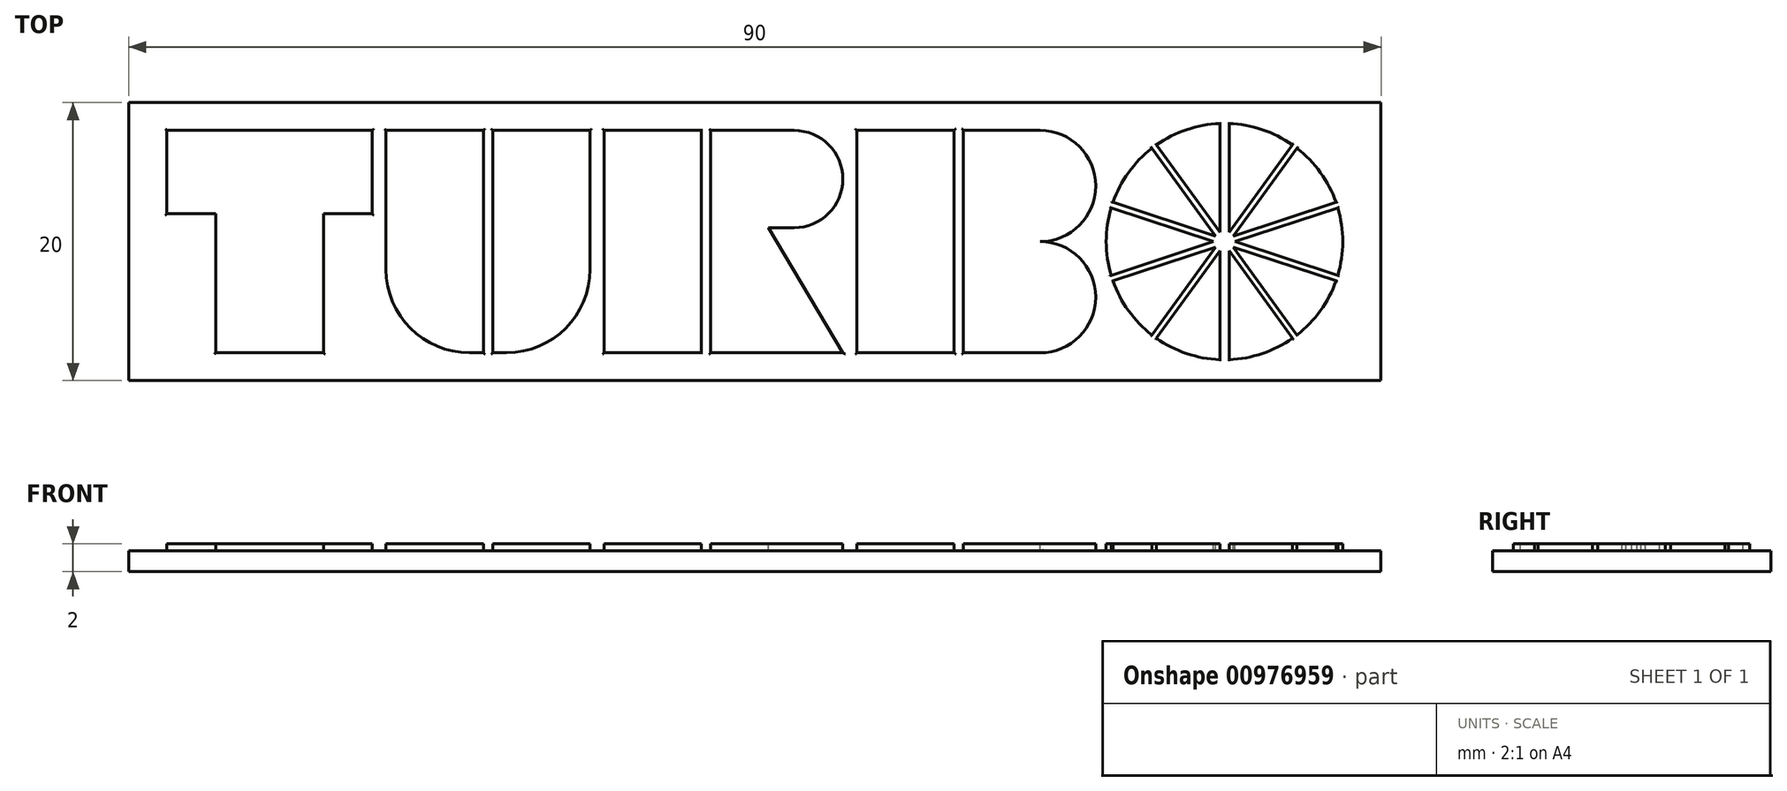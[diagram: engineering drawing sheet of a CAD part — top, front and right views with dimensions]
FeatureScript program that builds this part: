
annotation { "Feature Type Name" : "Feature", "Feature Type Description" : "" }
export const myFeature = defineFeature(function(context is Context, id is Id, definition is map)
    precondition{}
    {
        {
            var Q0;
            Q0=qCreatedBy(makeId("Top.planeOp"),FACE);
            var sketch = newSketch(context, id + "F0", { "sketchPlane" : qUnion([Q0])});
            skLineSegment(sketch, "E0.bottom", {"start": v(-37.82, -15.3) * mm, "end": v(52.18, -15.3) * mm});
            skLineSegment(sketch, "E0.top", {"start": v(-37.82, 4.7) * mm, "end": v(52.18, 4.7) * mm});
            skLineSegment(sketch, "E0.left", {"start": v(-37.82, -15.3) * mm, "end": v(-37.82, 4.7) * mm});
            skLineSegment(sketch, "E0.right", {"start": v(52.18, -15.3) * mm, "end": v(52.18, 4.7) * mm});
            skLineSegment(sketch, "E1", {"start": v(-20.58, -13.3) * mm, "end": v(-20.58, -7.3) * mm});
            skLineSegment(sketch, "E2", {"start": v(-20.58, -7.3) * mm, "end": v(-24.08, -7.3) * mm});
            skLineSegment(sketch, "E3", {"start": v(-24.08, -7.3) * mm, "end": v(-24.08, 2.7) * mm});
            skLineSegment(sketch, "E4", {"start": v(-24.08, 2.7) * mm, "end": v(-31.82, 2.7) * mm});
            skLineSegment(sketch, "E5", {"start": v(-31.82, 2.7) * mm, "end": v(-31.82, -7.3) * mm});
            skLineSegment(sketch, "E6", {"start": v(-31.82, -7.3) * mm, "end": v(-35.32, -7.3) * mm});
            skLineSegment(sketch, "E7", {"start": v(-35.32, -7.3) * mm, "end": v(-35.32, -13.3) * mm});
            skLineSegment(sketch, "E8", {"start": v(-35.32, -13.3) * mm, "end": v(-20.58, -13.3) * mm});
            skLineSegment(sketch, "E9.bottom", {"start": v(-19.58, -13.3) * mm, "end": v(-12.58, -13.3) * mm});
            skLineSegment(sketch, "E9.top", {"start": v(-13.58, 2.7) * mm, "end": v(-12.58, 2.7) * mm});
            skLineSegment(sketch, "E9.left", {"start": v(-19.58, -13.3) * mm, "end": v(-19.58, -3.3) * mm});
            skLineSegment(sketch, "E9.right", {"start": v(-12.58, -13.3) * mm, "end": v(-12.58, 2.7) * mm});
            skPoint(sketch, "E10.visualSharp", {"position": v(-19.58, 2.7) * mm});
            skArc(sketch, "E10.filletArc", {"start": v(-13.58, 2.7) * mm, "mid": v(-17.82, 0.94) * mm, "end": v(-19.58, -3.3) * mm});
            skLineSegment(sketch, "E11.bottom", {"start": v(-11.91, -13.3) * mm, "end": v(-4.91, -13.3) * mm});
            skLineSegment(sketch, "E11.top", {"start": v(-11.91, 2.7) * mm, "end": v(-10.91, 2.7) * mm});
            skLineSegment(sketch, "E11.left", {"start": v(-11.91, -13.3) * mm, "end": v(-11.91, 2.7) * mm});
            skLineSegment(sketch, "E11.right", {"start": v(-4.91, -13.3) * mm, "end": v(-4.91, -3.3) * mm});
            skPoint(sketch, "E12.visualSharp", {"position": v(-4.91, 2.7) * mm});
            skArc(sketch, "E12.filletArc", {"start": v(-4.91, -3.3) * mm, "mid": v(-6.67, 0.94) * mm, "end": v(-10.91, 2.7) * mm});
            skLineSegment(sketch, "E13.bottom", {"start": v(-3.91, -13.3) * mm, "end": v(3.09, -13.3) * mm});
            skLineSegment(sketch, "E13.top", {"start": v(-3.91, 2.7) * mm, "end": v(3.09, 2.7) * mm});
            skLineSegment(sketch, "E13.left", {"start": v(-3.91, -13.3) * mm, "end": v(-3.91, 2.7) * mm});
            skLineSegment(sketch, "E13.right", {"start": v(3.09, -13.3) * mm, "end": v(3.09, 2.7) * mm});
            skLineSegment(sketch, "E14", {"start": v(3.76, -13.3) * mm, "end": v(3.76, 2.7) * mm});
            skLineSegment(sketch, "E15", {"start": v(3.76, 2.7) * mm, "end": v(13.26, 2.7) * mm});
            skLineSegment(sketch, "E16", {"start": v(13.26, 2.7) * mm, "end": v(7.91, -6.3) * mm});
            skLineSegment(sketch, "E17.bottom", {"start": v(3.76, -13.3) * mm, "end": v(9.76, -13.3) * mm});
            skLineSegment(sketch, "E17.top", {"start": v(7.91, -6.3) * mm, "end": v(9.76, -6.3) * mm});
            skLineSegment(sketch, "E17.left", {"start": v(3.76, -13.3) * mm, "end": v(3.76, -6.3) * mm});
            skLineSegment(sketch, "E17.right", {"start": v(13.26, -9.8) * mm, "end": v(13.26, -9.8) * mm});
            skPoint(sketch, "E18.visualSharp", {"position": v(13.26, -13.3) * mm});
            skArc(sketch, "E18.filletArc", {"start": v(9.76, -13.3) * mm, "mid": v(12.23, -12.28) * mm, "end": v(13.26, -9.8) * mm});
            skPoint(sketch, "E19.visualSharp", {"position": v(13.26, -6.3) * mm});
            skArc(sketch, "E19.filletArc", {"start": v(13.26, -9.8) * mm, "mid": v(12.23, -7.33) * mm, "end": v(9.76, -6.3) * mm});
            skLineSegment(sketch, "E20.bottom", {"start": v(14.26, -13.3) * mm, "end": v(21.26, -13.3) * mm});
            skLineSegment(sketch, "E20.top", {"start": v(14.26, 2.7) * mm, "end": v(21.26, 2.7) * mm});
            skLineSegment(sketch, "E20.left", {"start": v(14.26, -13.3) * mm, "end": v(14.26, 2.7) * mm});
            skLineSegment(sketch, "E20.right", {"start": v(21.26, -13.3) * mm, "end": v(21.26, 2.7) * mm});
            skLineSegment(sketch, "E21.bottom", {"start": v(21.92, -13.3) * mm, "end": v(27.42, -13.3) * mm});
            skLineSegment(sketch, "E21.left", {"start": v(21.92, -13.3) * mm, "end": v(21.92, -5.3) * mm});
            skLineSegment(sketch, "E21.right", {"start": v(31.42, -9.3) * mm, "end": v(31.42, -9.3) * mm});
            skLineSegment(sketch, "E22.top", {"start": v(21.92, 2.7) * mm, "end": v(27.42, 2.7) * mm});
            skLineSegment(sketch, "E22.left", {"start": v(21.92, -5.3) * mm, "end": v(21.92, 2.7) * mm});
            skLineSegment(sketch, "E22.right", {"start": v(31.42, -1.3) * mm, "end": v(31.42, -1.3) * mm});
            skPoint(sketch, "E23.visualSharp", {"position": v(31.42, -13.3) * mm});
            skArc(sketch, "E23.filletArc", {"start": v(27.42, -13.3) * mm, "mid": v(30.25, -12.14) * mm, "end": v(31.42, -9.3) * mm});
            skPoint(sketch, "E24.visualSharp", {"position": v(31.42, -5.3) * mm});
            skArc(sketch, "E24.filletArc", {"start": v(31.42, -9.3) * mm, "mid": v(30.25, -6.48) * mm, "end": v(27.42, -5.3) * mm});
            skArc(sketch, "E25.filletArc", {"start": v(27.42, -5.3) * mm, "mid": v(30.25, -4.14) * mm, "end": v(31.42, -1.3) * mm});
            skPoint(sketch, "E26.visualSharp", {"position": v(31.42, 2.7) * mm});
            skArc(sketch, "E26.filletArc", {"start": v(31.42, -1.3) * mm, "mid": v(30.25, 1.52) * mm, "end": v(27.42, 2.7) * mm});
            skArc(sketch, "E27", {"start": v(41.01, -13.8) * mm, "mid": v(43.4, -13.36) * mm, "end": v(45.56, -12.27) * mm});
            skArc(sketch, "E28", {"start": v(39.93, -5.3) * mm, "mid": v(39.93, -5.3) * mm, "end": v(39.93, -5.32) * mm});
            skLineSegment(sketch, "E29", {"start": v(40.68, 4.7) * mm, "end": v(40.68, 8.95) * mm, "construction": true});
            skLineSegment(sketch, "E30.left", {"start": v(40.34, -13.8) * mm, "end": v(40.34, -5.98) * mm});
            skLineSegment(sketch, "E30.right", {"start": v(41.01, -13.8) * mm, "end": v(41.01, -5.98) * mm});
            skLineSegment(sketch, "E31.trimOffspring", {"start": v(40.34, -4.64) * mm, "end": v(40.34, 3.19) * mm});
            skLineSegment(sketch, "E32.trimOffspring", {"start": v(41.01, -4.64) * mm, "end": v(41.01, 3.19) * mm});
            skArc(sketch, "E33.trimOffspring", {"start": v(40.34, 3.19) * mm, "mid": v(37.96, 2.75) * mm, "end": v(35.8, 1.65) * mm});
            skLineSegment(sketch, "E34", {"start": v(41.01, -4.64) * mm, "end": v(45.56, 1.65) * mm});
            skLineSegment(sketch, "E35", {"start": v(41.01, -5.98) * mm, "end": v(45.56, -12.27) * mm});
            skLineSegment(sketch, "E36", {"start": v(40.34, -5.98) * mm, "end": v(35.8, -12.27) * mm});
            skLineSegment(sketch, "E37", {"start": v(40.34, -4.64) * mm, "end": v(35.8, 1.65) * mm});
            skLineSegment(sketch, "E38", {"start": v(41.31, -4.91) * mm, "end": v(45.89, 1.4) * mm});
            skLineSegment(sketch, "E39", {"start": v(41.31, -4.91) * mm, "end": v(48.7, -2.49) * mm});
            skLineSegment(sketch, "E40", {"start": v(40.04, -4.91) * mm, "end": v(35.47, 1.4) * mm});
            skLineSegment(sketch, "E41", {"start": v(40.04, -4.91) * mm, "end": v(32.66, -2.49) * mm});
            skLineSegment(sketch, "E42", {"start": v(45.89, -12.02) * mm, "end": v(41.31, -5.7) * mm});
            skLineSegment(sketch, "E43", {"start": v(40.04, -5.7) * mm, "end": v(35.47, -12.02) * mm});
            skLineSegment(sketch, "E44", {"start": v(41.31, -5.7) * mm, "end": v(48.7, -8.13) * mm});
            skLineSegment(sketch, "E45", {"start": v(40.04, -5.7) * mm, "end": v(32.66, -8.13) * mm});
            skLineSegment(sketch, "E46", {"start": v(41.43, -5.3) * mm, "end": v(48.82, -7.74) * mm});
            skLineSegment(sketch, "E47", {"start": v(41.43, -5.3) * mm, "end": v(48.82, -2.87) * mm});
            skLineSegment(sketch, "E48", {"start": v(39.93, -5.3) * mm, "end": v(32.53, -7.73) * mm});
            skLineSegment(sketch, "E49", {"start": v(32.53, -2.89) * mm, "end": v(39.93, -5.32) * mm});
            skArc(sketch, "E50.trimOffspring", {"start": v(35.8, -12.27) * mm, "mid": v(37.96, -13.36) * mm, "end": v(40.34, -13.8) * mm});
            skArc(sketch, "E51.trimOffspring", {"start": v(32.66, -8.13) * mm, "mid": v(33.78, -10.28) * mm, "end": v(35.47, -12.02) * mm});
            skArc(sketch, "E52.trimOffspring", {"start": v(32.53, -2.89) * mm, "mid": v(32.18, -5.3) * mm, "end": v(32.53, -7.73) * mm});
            skArc(sketch, "E53.trimOffspring", {"start": v(45.89, -12.02) * mm, "mid": v(47.57, -10.28) * mm, "end": v(48.7, -8.13) * mm});
            skArc(sketch, "E54.trimOffspring", {"start": v(48.82, -7.74) * mm, "mid": v(49.18, -5.3) * mm, "end": v(48.82, -2.87) * mm});
            skArc(sketch, "E55.trimOffspring", {"start": v(48.7, -2.49) * mm, "mid": v(47.57, -0.34) * mm, "end": v(45.89, 1.4) * mm});
            skArc(sketch, "E56.trimOffspring", {"start": v(45.56, 1.65) * mm, "mid": v(43.4, 2.75) * mm, "end": v(41.01, 3.19) * mm});
            skArc(sketch, "E57.trimOffspring", {"start": v(35.47, 1.4) * mm, "mid": v(33.78, -0.34) * mm, "end": v(32.66, -2.49) * mm});
            skSolve(sketch);
        }
        {
            var Q0;
            Q0=makeQuery(id+"F0.imprint","IMPRINT",FACE,{"disambiguationData":[TD([[makeQuery(id+"F0.imprint","IMPRINT",EDGE,{"derivedFrom":sQuery(id+"F0.wireOp",EDGE,"E1")}),1.0]])]});
            var Q1;
            Q1=makeQuery(id+"F0.imprint","IMPRINT",FACE,{"disambiguationData":[TD([[makeQuery(id+"F0.imprint","IMPRINT",EDGE,{"derivedFrom":sQuery(id+"F0.wireOp",EDGE,"E9.bottom")}),1.0]])]});
            var Q2;
            Q2=makeQuery(id+"F0.imprint","IMPRINT",FACE,{"disambiguationData":[TD([[makeQuery(id+"F0.imprint","IMPRINT",EDGE,{"derivedFrom":sQuery(id+"F0.wireOp",EDGE,"E11.bottom")}),1.0]])]});
            var Q3;
            Q3=makeQuery(id+"F0.imprint","IMPRINT",FACE,{"disambiguationData":[TD([[makeQuery(id+"F0.imprint","IMPRINT",EDGE,{"derivedFrom":sQuery(id+"F0.wireOp",EDGE,"E13.bottom")}),1.0]])]});
            var Q4;
            Q4=makeQuery(id+"F0.imprint","IMPRINT",FACE,{"disambiguationData":[TD([[makeQuery(id+"F0.imprint","IMPRINT",EDGE,{"derivedFrom":sQuery(id+"F0.wireOp",EDGE,"E14")}),-1.0]])]});
            var Q5;
            Q5=makeQuery(id+"F0.imprint","IMPRINT",FACE,{"disambiguationData":[TD([[makeQuery(id+"F0.imprint","IMPRINT",EDGE,{"derivedFrom":sQuery(id+"F0.wireOp",EDGE,"E20.bottom")}),1.0]])]});
            var Q6;
            Q6=makeQuery(id+"F0.imprint","IMPRINT",FACE,{"disambiguationData":[TD([[makeQuery(id+"F0.imprint","IMPRINT",EDGE,{"derivedFrom":sQuery(id+"F0.wireOp",EDGE,"E22.bottom")}),1.0]])]});
            var Q7;
            Q7=makeQuery(id+"F0.imprint","IMPRINT",FACE,{"disambiguationData":[TD([[makeQuery(id+"F0.imprint","IMPRINT",EDGE,{"derivedFrom":sQuery(id+"F0.wireOp",EDGE,"E21.bottom")}),1.0]])]});
            var Q8;
            Q8=makeQuery(id+"F0.imprint","IMPRINT",FACE,{"disambiguationData":[TD([[makeQuery(id+"F0.imprint","IMPRINT",EDGE,{"derivedFrom":sQuery(id+"F0.wireOp",EDGE,"E31.trimOffspring")}),1.0]])]});
            var Q9;
            Q9=makeQuery(id+"F0.imprint","IMPRINT",FACE,{"disambiguationData":[TD([[makeQuery(id+"F0.imprint","IMPRINT",EDGE,{"derivedFrom":sQuery(id+"F0.wireOp",EDGE,"E40")}),1.0]])]});
            var Q10;
            {var subQ0=sQuery(id+"F0.wireOp",EDGE,"E52.trimOffspring");Q10=makeQuery(id+"F0.imprint","IMPRINT",FACE,{"disambiguationData":[TD([[makeQuery(id+"F0.imprint","IMPRINT",EDGE,{"derivedFrom":subQ0}),1.0]])]});}
            var Q11;
            Q11=makeQuery(id+"F0.imprint","IMPRINT",FACE,{"disambiguationData":[TD([[makeQuery(id+"F0.imprint","IMPRINT",EDGE,{"derivedFrom":sQuery(id+"F0.wireOp",EDGE,"E43")}),-1.0]])]});
            var Q12;
            Q12=makeQuery(id+"F0.imprint","IMPRINT",FACE,{"disambiguationData":[TD([[makeQuery(id+"F0.imprint","IMPRINT",EDGE,{"derivedFrom":sQuery(id+"F0.wireOp",EDGE,"E30.left")}),1.0]])]});
            var Q13;
            Q13=makeQuery(id+"F0.imprint","IMPRINT",FACE,{"disambiguationData":[TD([[makeQuery(id+"F0.imprint","IMPRINT",EDGE,{"derivedFrom":sQuery(id+"F0.wireOp",EDGE,"E27")}),1.0]])]});
            var Q14;
            Q14=makeQuery(id+"F0.imprint","IMPRINT",FACE,{"disambiguationData":[TD([[makeQuery(id+"F0.imprint","IMPRINT",EDGE,{"derivedFrom":sQuery(id+"F0.wireOp",EDGE,"E42")}),-1.0]])]});
            var Q15;
            Q15=makeQuery(id+"F0.imprint","IMPRINT",FACE,{"disambiguationData":[TD([[makeQuery(id+"F0.imprint","IMPRINT",EDGE,{"derivedFrom":sQuery(id+"F0.wireOp",EDGE,"E46")}),1.0]])]});
            var Q16;
            Q16=makeQuery(id+"F0.imprint","IMPRINT",FACE,{"disambiguationData":[TD([[makeQuery(id+"F0.imprint","IMPRINT",EDGE,{"derivedFrom":sQuery(id+"F0.wireOp",EDGE,"E38")}),-1.0]])]});
            var Q17;
            Q17=makeQuery(id+"F0.imprint","IMPRINT",FACE,{"disambiguationData":[TD([[makeQuery(id+"F0.imprint","IMPRINT",EDGE,{"derivedFrom":sQuery(id+"F0.wireOp",EDGE,"E32.trimOffspring")}),-1.0]])]});
            extrude(context, id + "F1", {"entities" : qUnion([Q0, Q1, Q2, Q3, Q4, Q5, Q6, Q7, Q8, Q9, Q10, Q11, Q12, Q13, Q14, Q15, Q16, Q17]), "depth" : 2 * mm, "offsetDistance" : 25 * mm});
        }
        {
            var Q0;
            Q0=makeQuery(id+"F1.opExtrude","CAP_FACE",FACE,{"disambiguationData":[OSD([sQuery(id+"F0.wireOp",EDGE,"E20.bottom"),sQuery(id+"F0.wireOp",EDGE,"E20.top"),sQuery(id+"F0.wireOp",EDGE,"E20.left"),sQuery(id+"F0.wireOp",EDGE,"E20.right")])],"isStart":false});
            cPlane(context, id + "F2", {"entities" : qUnion([Q0]), "cplaneType" : CPlaneType.OFFSET, "offset" : 0 * mm, "width" : 150 * mm, "height" : 150 * mm});
        }
        {
            var Q0;
            Q0=qCreatedBy(id+"F2.planeOp",FACE);
            var sketch = newSketch(context, id + "F3", { "sketchPlane" : qUnion([Q0])});
            skLineSegment(sketch, "E58.bottom", {"start": v(-38.07, 4.7) * mm, "end": v(51.93, 4.7) * mm});
            skLineSegment(sketch, "E58.top", {"start": v(-38.07, -15.3) * mm, "end": v(51.93, -15.3) * mm});
            skLineSegment(sketch, "E58.left", {"start": v(-38.07, 4.7) * mm, "end": v(-38.07, -15.3) * mm});
            skLineSegment(sketch, "E58.right", {"start": v(51.93, 4.7) * mm, "end": v(51.93, -15.3) * mm});
            skSolve(sketch);
        }
        {
            var Q0;
            Q0 = qSketchRegion(id + "F3", true);
            extrude(context, id + "F4", {"entities" : qUnion([Q0]), "depth" : -1.5 * mm, "offsetDistance" : 25 * mm});
        }
        {
            var Q0;
            Q0=makeQuery(id+"F1.opExtrude","SWEPT_BODY",BODY,{"disambiguationData":[OSD([sQuery(id+"F0.wireOp",EDGE,"E1"),sQuery(id+"F0.wireOp",EDGE,"E2"),sQuery(id+"F0.wireOp",EDGE,"E3"),sQuery(id+"F0.wireOp",EDGE,"E4"),sQuery(id+"F0.wireOp",EDGE,"E5"),sQuery(id+"F0.wireOp",EDGE,"E6"),sQuery(id+"F0.wireOp",EDGE,"E7"),sQuery(id+"F0.wireOp",EDGE,"E8")])]});
            var Q1;
            Q1=makeQuery(id+"F1.opExtrude","SWEPT_BODY",BODY,{"disambiguationData":[OSD([sQuery(id+"F0.wireOp",EDGE,"E9.bottom"),sQuery(id+"F0.wireOp",EDGE,"E9.top"),sQuery(id+"F0.wireOp",EDGE,"E9.left"),sQuery(id+"F0.wireOp",EDGE,"E9.right"),sQuery(id+"F0.wireOp",EDGE,"E10.filletArc")])]});
            var Q2;
            Q2=makeQuery(id+"F1.opExtrude","SWEPT_BODY",BODY,{"disambiguationData":[OSD([sQuery(id+"F0.wireOp",EDGE,"E11.bottom"),sQuery(id+"F0.wireOp",EDGE,"E11.top"),sQuery(id+"F0.wireOp",EDGE,"E11.left"),sQuery(id+"F0.wireOp",EDGE,"E11.right"),sQuery(id+"F0.wireOp",EDGE,"E12.filletArc")])]});
            var Q3;
            Q3=makeQuery(id+"F1.opExtrude","SWEPT_BODY",BODY,{"disambiguationData":[OSD([sQuery(id+"F0.wireOp",EDGE,"E13.bottom"),sQuery(id+"F0.wireOp",EDGE,"E13.top"),sQuery(id+"F0.wireOp",EDGE,"E13.left"),sQuery(id+"F0.wireOp",EDGE,"E13.right")])]});
            var Q4;
            Q4=makeQuery(id+"F1.opExtrude","SWEPT_BODY",BODY,{"disambiguationData":[OSD([sQuery(id+"F0.wireOp",EDGE,"E14"),sQuery(id+"F0.wireOp",EDGE,"E15"),sQuery(id+"F0.wireOp",EDGE,"E16"),sQuery(id+"F0.wireOp",EDGE,"E17.bottom"),sQuery(id+"F0.wireOp",EDGE,"E17.top"),sQuery(id+"F0.wireOp",EDGE,"E17.left"),sQuery(id+"F0.wireOp",EDGE,"E18.filletArc"),sQuery(id+"F0.wireOp",EDGE,"E19.filletArc")])]});
            var Q5;
            Q5=makeQuery(id+"F1.opExtrude","SWEPT_BODY",BODY,{"disambiguationData":[OSD([sQuery(id+"F0.wireOp",EDGE,"E20.bottom"),sQuery(id+"F0.wireOp",EDGE,"E20.top"),sQuery(id+"F0.wireOp",EDGE,"E20.left"),sQuery(id+"F0.wireOp",EDGE,"E20.right")])]});
            var Q6;
            Q6=makeQuery(id+"F1.opExtrude","SWEPT_BODY",BODY,{"disambiguationData":[OSD([sQuery(id+"F0.wireOp",EDGE,"E21.bottom"),sQuery(id+"F0.wireOp",EDGE,"E21.left"),sQuery(id+"F0.wireOp",EDGE,"E22.top"),sQuery(id+"F0.wireOp",EDGE,"E22.left"),sQuery(id+"F0.wireOp",EDGE,"E23.filletArc"),sQuery(id+"F0.wireOp",EDGE,"E24.filletArc"),sQuery(id+"F0.wireOp",EDGE,"E25.filletArc"),sQuery(id+"F0.wireOp",EDGE,"E26.filletArc")])]});
            var Q7;
            Q7=makeQuery(id+"F1.opExtrude","SWEPT_BODY",BODY,{"disambiguationData":[OSD([sQuery(id+"F0.wireOp",EDGE,"E27"),sQuery(id+"F0.wireOp",EDGE,"E30.right"),sQuery(id+"F0.wireOp",EDGE,"E35")])]});
            var Q8;
            Q8=makeQuery(id+"F1.opExtrude","SWEPT_BODY",BODY,{"disambiguationData":[OSD([sQuery(id+"F0.wireOp",EDGE,"E30.left"),sQuery(id+"F0.wireOp",EDGE,"E36"),sQuery(id+"F0.wireOp",EDGE,"E50.trimOffspring")])]});
            var Q9;
            Q9=makeQuery(id+"F1.opExtrude","SWEPT_BODY",BODY,{"disambiguationData":[OSD([sQuery(id+"F0.wireOp",EDGE,"E31.trimOffspring"),sQuery(id+"F0.wireOp",EDGE,"E33.trimOffspring"),sQuery(id+"F0.wireOp",EDGE,"E37")])]});
            var Q10;
            Q10=makeQuery(id+"F1.opExtrude","SWEPT_BODY",BODY,{"disambiguationData":[OSD([sQuery(id+"F0.wireOp",EDGE,"E32.trimOffspring"),sQuery(id+"F0.wireOp",EDGE,"E34"),sQuery(id+"F0.wireOp",EDGE,"E56.trimOffspring")])]});
            var Q11;
            Q11=makeQuery(id+"F1.opExtrude","SWEPT_BODY",BODY,{"disambiguationData":[OSD([sQuery(id+"F0.wireOp",EDGE,"E38"),sQuery(id+"F0.wireOp",EDGE,"E39"),sQuery(id+"F0.wireOp",EDGE,"E55.trimOffspring")])]});
            var Q12;
            Q12=makeQuery(id+"F1.opExtrude","SWEPT_BODY",BODY,{"disambiguationData":[OSD([sQuery(id+"F0.wireOp",EDGE,"E40"),sQuery(id+"F0.wireOp",EDGE,"E41"),sQuery(id+"F0.wireOp",EDGE,"E57.trimOffspring")])]});
            var Q13;
            Q13=makeQuery(id+"F1.opExtrude","SWEPT_BODY",BODY,{"disambiguationData":[OSD([sQuery(id+"F0.wireOp",EDGE,"E42"),sQuery(id+"F0.wireOp",EDGE,"E44"),sQuery(id+"F0.wireOp",EDGE,"E53.trimOffspring")])]});
            var Q14;
            Q14=makeQuery(id+"F1.opExtrude","SWEPT_BODY",BODY,{"disambiguationData":[OSD([sQuery(id+"F0.wireOp",EDGE,"E43"),sQuery(id+"F0.wireOp",EDGE,"E45"),sQuery(id+"F0.wireOp",EDGE,"E51.trimOffspring")])]});
            var Q15;
            Q15=makeQuery(id+"F1.opExtrude","SWEPT_BODY",BODY,{"disambiguationData":[OSD([sQuery(id+"F0.wireOp",EDGE,"E46"),sQuery(id+"F0.wireOp",EDGE,"E47"),sQuery(id+"F0.wireOp",EDGE,"E54.trimOffspring")])]});
            var Q16;
            Q16=makeQuery(id+"F1.opExtrude","SWEPT_BODY",BODY,{"disambiguationData":[OSD([sQuery(id+"F0.wireOp",EDGE,"E48"),sQuery(id+"F0.wireOp",EDGE,"E49"),sQuery(id+"F0.wireOp",EDGE,"E52.trimOffspring")])]});
            var Q17;
            Q17=makeQuery(id+"F4.opExtrude","SWEPT_BODY",BODY,{"disambiguationData":[OSD([sQuery(id+"F3.wireOp",EDGE,"E58.bottom"),sQuery(id+"F3.wireOp",EDGE,"E58.top"),sQuery(id+"F3.wireOp",EDGE,"E58.left"),sQuery(id+"F3.wireOp",EDGE,"E58.right")])]});
            transform(context, id + "F5", {"entities" : qUnion([Q0, Q1, Q2, Q3, Q4, Q5, Q6, Q7, Q8, Q9, Q10, Q11, Q12, Q13, Q14, Q15, Q16, Q17]), "transformType" : TransformType.TRANSLATION_3D, "dx" : 0 * mm, "dy" : 0 * mm, "dz" : 0 * mm, "makeCopy" : false});
        }
        {
            var Q0;
            Q0=makeQuery(id+"F1.opExtrude","SWEPT_BODY",BODY,{"disambiguationData":[OSD([sQuery(id+"F0.wireOp",EDGE,"E1"),sQuery(id+"F0.wireOp",EDGE,"E2"),sQuery(id+"F0.wireOp",EDGE,"E3"),sQuery(id+"F0.wireOp",EDGE,"E4"),sQuery(id+"F0.wireOp",EDGE,"E5"),sQuery(id+"F0.wireOp",EDGE,"E6"),sQuery(id+"F0.wireOp",EDGE,"E7"),sQuery(id+"F0.wireOp",EDGE,"E8")])]});
            var Q1;
            Q1=makeQuery(id+"F1.opExtrude","SWEPT_BODY",BODY,{"disambiguationData":[OSD([sQuery(id+"F0.wireOp",EDGE,"E9.bottom"),sQuery(id+"F0.wireOp",EDGE,"E9.top"),sQuery(id+"F0.wireOp",EDGE,"E9.left"),sQuery(id+"F0.wireOp",EDGE,"E9.right"),sQuery(id+"F0.wireOp",EDGE,"E10.filletArc")])]});
            var Q2;
            Q2=makeQuery(id+"F1.opExtrude","SWEPT_BODY",BODY,{"disambiguationData":[OSD([sQuery(id+"F0.wireOp",EDGE,"E11.bottom"),sQuery(id+"F0.wireOp",EDGE,"E11.top"),sQuery(id+"F0.wireOp",EDGE,"E11.left"),sQuery(id+"F0.wireOp",EDGE,"E11.right"),sQuery(id+"F0.wireOp",EDGE,"E12.filletArc")])]});
            var Q3;
            Q3=makeQuery(id+"F1.opExtrude","SWEPT_BODY",BODY,{"disambiguationData":[OSD([sQuery(id+"F0.wireOp",EDGE,"E13.bottom"),sQuery(id+"F0.wireOp",EDGE,"E13.top"),sQuery(id+"F0.wireOp",EDGE,"E13.left"),sQuery(id+"F0.wireOp",EDGE,"E13.right")])]});
            var Q4;
            Q4=makeQuery(id+"F1.opExtrude","SWEPT_BODY",BODY,{"disambiguationData":[OSD([sQuery(id+"F0.wireOp",EDGE,"E14"),sQuery(id+"F0.wireOp",EDGE,"E15"),sQuery(id+"F0.wireOp",EDGE,"E16"),sQuery(id+"F0.wireOp",EDGE,"E17.bottom"),sQuery(id+"F0.wireOp",EDGE,"E17.top"),sQuery(id+"F0.wireOp",EDGE,"E17.left"),sQuery(id+"F0.wireOp",EDGE,"E18.filletArc"),sQuery(id+"F0.wireOp",EDGE,"E19.filletArc")])]});
            var Q5;
            Q5=makeQuery(id+"F1.opExtrude","SWEPT_BODY",BODY,{"disambiguationData":[OSD([sQuery(id+"F0.wireOp",EDGE,"E20.bottom"),sQuery(id+"F0.wireOp",EDGE,"E20.top"),sQuery(id+"F0.wireOp",EDGE,"E20.left"),sQuery(id+"F0.wireOp",EDGE,"E20.right")])]});
            var Q6;
            Q6=makeQuery(id+"F1.opExtrude","SWEPT_BODY",BODY,{"disambiguationData":[OSD([sQuery(id+"F0.wireOp",EDGE,"E21.bottom"),sQuery(id+"F0.wireOp",EDGE,"E21.left"),sQuery(id+"F0.wireOp",EDGE,"E22.top"),sQuery(id+"F0.wireOp",EDGE,"E22.left"),sQuery(id+"F0.wireOp",EDGE,"E23.filletArc"),sQuery(id+"F0.wireOp",EDGE,"E24.filletArc"),sQuery(id+"F0.wireOp",EDGE,"E25.filletArc"),sQuery(id+"F0.wireOp",EDGE,"E26.filletArc")])]});
            var Q7;
            Q7=makeQuery(id+"F1.opExtrude","SWEPT_BODY",BODY,{"disambiguationData":[OSD([sQuery(id+"F0.wireOp",EDGE,"E27"),sQuery(id+"F0.wireOp",EDGE,"E30.right"),sQuery(id+"F0.wireOp",EDGE,"E35")])]});
            var Q8;
            Q8=makeQuery(id+"F1.opExtrude","SWEPT_BODY",BODY,{"disambiguationData":[OSD([sQuery(id+"F0.wireOp",EDGE,"E30.left"),sQuery(id+"F0.wireOp",EDGE,"E36"),sQuery(id+"F0.wireOp",EDGE,"E50.trimOffspring")])]});
            var Q9;
            Q9=makeQuery(id+"F1.opExtrude","SWEPT_BODY",BODY,{"disambiguationData":[OSD([sQuery(id+"F0.wireOp",EDGE,"E31.trimOffspring"),sQuery(id+"F0.wireOp",EDGE,"E33.trimOffspring"),sQuery(id+"F0.wireOp",EDGE,"E37")])]});
            var Q10;
            Q10=makeQuery(id+"F1.opExtrude","SWEPT_BODY",BODY,{"disambiguationData":[OSD([sQuery(id+"F0.wireOp",EDGE,"E32.trimOffspring"),sQuery(id+"F0.wireOp",EDGE,"E34"),sQuery(id+"F0.wireOp",EDGE,"E56.trimOffspring")])]});
            var Q11;
            Q11=makeQuery(id+"F1.opExtrude","SWEPT_BODY",BODY,{"disambiguationData":[OSD([sQuery(id+"F0.wireOp",EDGE,"E38"),sQuery(id+"F0.wireOp",EDGE,"E39"),sQuery(id+"F0.wireOp",EDGE,"E55.trimOffspring")])]});
            var Q12;
            Q12=makeQuery(id+"F1.opExtrude","SWEPT_BODY",BODY,{"disambiguationData":[OSD([sQuery(id+"F0.wireOp",EDGE,"E40"),sQuery(id+"F0.wireOp",EDGE,"E41"),sQuery(id+"F0.wireOp",EDGE,"E57.trimOffspring")])]});
            var Q13;
            Q13=makeQuery(id+"F1.opExtrude","SWEPT_BODY",BODY,{"disambiguationData":[OSD([sQuery(id+"F0.wireOp",EDGE,"E42"),sQuery(id+"F0.wireOp",EDGE,"E44"),sQuery(id+"F0.wireOp",EDGE,"E53.trimOffspring")])]});
            var Q14;
            Q14=makeQuery(id+"F1.opExtrude","SWEPT_BODY",BODY,{"disambiguationData":[OSD([sQuery(id+"F0.wireOp",EDGE,"E43"),sQuery(id+"F0.wireOp",EDGE,"E45"),sQuery(id+"F0.wireOp",EDGE,"E51.trimOffspring")])]});
            var Q15;
            Q15=makeQuery(id+"F1.opExtrude","SWEPT_BODY",BODY,{"disambiguationData":[OSD([sQuery(id+"F0.wireOp",EDGE,"E46"),sQuery(id+"F0.wireOp",EDGE,"E47"),sQuery(id+"F0.wireOp",EDGE,"E54.trimOffspring")])]});
            var Q16;
            Q16=makeQuery(id+"F1.opExtrude","SWEPT_BODY",BODY,{"disambiguationData":[OSD([sQuery(id+"F0.wireOp",EDGE,"E48"),sQuery(id+"F0.wireOp",EDGE,"E49"),sQuery(id+"F0.wireOp",EDGE,"E52.trimOffspring")])]});
            var Q17;
            Q17=makeQuery(id+"F4.opExtrude","SWEPT_BODY",BODY,{"disambiguationData":[OSD([sQuery(id+"F3.wireOp",EDGE,"E58.bottom"),sQuery(id+"F3.wireOp",EDGE,"E58.top"),sQuery(id+"F3.wireOp",EDGE,"E58.left"),sQuery(id+"F3.wireOp",EDGE,"E58.right")])]});
            transform(context, id + "F6", {"entities" : qUnion([Q0, Q1, Q2, Q3, Q4, Q5, Q6, Q7, Q8, Q9, Q10, Q11, Q12, Q13, Q14, Q15, Q16, Q17]), "transformType" : TransformType.TRANSLATION_3D, "dx" : -3.1 * mm, "dy" : -2.4 * mm, "dz" : 9.9 * mm, "makeCopy" : false});
        }
        {
            var Q0;
            Q0=makeQuery(id+"F1.opExtrude","SWEPT_BODY",BODY,{"disambiguationData":[OSD([sQuery(id+"F0.wireOp",EDGE,"E1"),sQuery(id+"F0.wireOp",EDGE,"E2"),sQuery(id+"F0.wireOp",EDGE,"E3"),sQuery(id+"F0.wireOp",EDGE,"E4"),sQuery(id+"F0.wireOp",EDGE,"E5"),sQuery(id+"F0.wireOp",EDGE,"E6"),sQuery(id+"F0.wireOp",EDGE,"E7"),sQuery(id+"F0.wireOp",EDGE,"E8")])]});
            var Q1;
            Q1=makeQuery(id+"F1.opExtrude","SWEPT_BODY",BODY,{"disambiguationData":[OSD([sQuery(id+"F0.wireOp",EDGE,"E9.bottom"),sQuery(id+"F0.wireOp",EDGE,"E9.top"),sQuery(id+"F0.wireOp",EDGE,"E9.left"),sQuery(id+"F0.wireOp",EDGE,"E9.right"),sQuery(id+"F0.wireOp",EDGE,"E10.filletArc")])]});
            var Q2;
            Q2=makeQuery(id+"F1.opExtrude","SWEPT_BODY",BODY,{"disambiguationData":[OSD([sQuery(id+"F0.wireOp",EDGE,"E11.bottom"),sQuery(id+"F0.wireOp",EDGE,"E11.top"),sQuery(id+"F0.wireOp",EDGE,"E11.left"),sQuery(id+"F0.wireOp",EDGE,"E11.right"),sQuery(id+"F0.wireOp",EDGE,"E12.filletArc")])]});
            var Q3;
            Q3=makeQuery(id+"F1.opExtrude","SWEPT_BODY",BODY,{"disambiguationData":[OSD([sQuery(id+"F0.wireOp",EDGE,"E13.bottom"),sQuery(id+"F0.wireOp",EDGE,"E13.top"),sQuery(id+"F0.wireOp",EDGE,"E13.left"),sQuery(id+"F0.wireOp",EDGE,"E13.right")])]});
            var Q4;
            Q4=makeQuery(id+"F1.opExtrude","SWEPT_BODY",BODY,{"disambiguationData":[OSD([sQuery(id+"F0.wireOp",EDGE,"E14"),sQuery(id+"F0.wireOp",EDGE,"E15"),sQuery(id+"F0.wireOp",EDGE,"E16"),sQuery(id+"F0.wireOp",EDGE,"E17.bottom"),sQuery(id+"F0.wireOp",EDGE,"E17.top"),sQuery(id+"F0.wireOp",EDGE,"E17.left"),sQuery(id+"F0.wireOp",EDGE,"E18.filletArc"),sQuery(id+"F0.wireOp",EDGE,"E19.filletArc")])]});
            var Q5;
            Q5=makeQuery(id+"F1.opExtrude","SWEPT_BODY",BODY,{"disambiguationData":[OSD([sQuery(id+"F0.wireOp",EDGE,"E20.bottom"),sQuery(id+"F0.wireOp",EDGE,"E20.top"),sQuery(id+"F0.wireOp",EDGE,"E20.left"),sQuery(id+"F0.wireOp",EDGE,"E20.right")])]});
            var Q6;
            Q6=makeQuery(id+"F1.opExtrude","SWEPT_BODY",BODY,{"disambiguationData":[OSD([sQuery(id+"F0.wireOp",EDGE,"E21.bottom"),sQuery(id+"F0.wireOp",EDGE,"E21.left"),sQuery(id+"F0.wireOp",EDGE,"E22.top"),sQuery(id+"F0.wireOp",EDGE,"E22.left"),sQuery(id+"F0.wireOp",EDGE,"E23.filletArc"),sQuery(id+"F0.wireOp",EDGE,"E24.filletArc"),sQuery(id+"F0.wireOp",EDGE,"E25.filletArc"),sQuery(id+"F0.wireOp",EDGE,"E26.filletArc")])]});
            var Q7;
            Q7=makeQuery(id+"F1.opExtrude","SWEPT_BODY",BODY,{"disambiguationData":[OSD([sQuery(id+"F0.wireOp",EDGE,"E27"),sQuery(id+"F0.wireOp",EDGE,"E30.right"),sQuery(id+"F0.wireOp",EDGE,"E35")])]});
            var Q8;
            Q8=makeQuery(id+"F1.opExtrude","SWEPT_BODY",BODY,{"disambiguationData":[OSD([sQuery(id+"F0.wireOp",EDGE,"E30.left"),sQuery(id+"F0.wireOp",EDGE,"E36"),sQuery(id+"F0.wireOp",EDGE,"E50.trimOffspring")])]});
            var Q9;
            Q9=makeQuery(id+"F1.opExtrude","SWEPT_BODY",BODY,{"disambiguationData":[OSD([sQuery(id+"F0.wireOp",EDGE,"E31.trimOffspring"),sQuery(id+"F0.wireOp",EDGE,"E33.trimOffspring"),sQuery(id+"F0.wireOp",EDGE,"E37")])]});
            var Q10;
            Q10=makeQuery(id+"F1.opExtrude","SWEPT_BODY",BODY,{"disambiguationData":[OSD([sQuery(id+"F0.wireOp",EDGE,"E32.trimOffspring"),sQuery(id+"F0.wireOp",EDGE,"E34"),sQuery(id+"F0.wireOp",EDGE,"E56.trimOffspring")])]});
            var Q11;
            Q11=makeQuery(id+"F1.opExtrude","SWEPT_BODY",BODY,{"disambiguationData":[OSD([sQuery(id+"F0.wireOp",EDGE,"E38"),sQuery(id+"F0.wireOp",EDGE,"E39"),sQuery(id+"F0.wireOp",EDGE,"E55.trimOffspring")])]});
            var Q12;
            Q12=makeQuery(id+"F1.opExtrude","SWEPT_BODY",BODY,{"disambiguationData":[OSD([sQuery(id+"F0.wireOp",EDGE,"E40"),sQuery(id+"F0.wireOp",EDGE,"E41"),sQuery(id+"F0.wireOp",EDGE,"E57.trimOffspring")])]});
            var Q13;
            Q13=makeQuery(id+"F1.opExtrude","SWEPT_BODY",BODY,{"disambiguationData":[OSD([sQuery(id+"F0.wireOp",EDGE,"E42"),sQuery(id+"F0.wireOp",EDGE,"E44"),sQuery(id+"F0.wireOp",EDGE,"E53.trimOffspring")])]});
            var Q14;
            Q14=makeQuery(id+"F1.opExtrude","SWEPT_BODY",BODY,{"disambiguationData":[OSD([sQuery(id+"F0.wireOp",EDGE,"E43"),sQuery(id+"F0.wireOp",EDGE,"E45"),sQuery(id+"F0.wireOp",EDGE,"E51.trimOffspring")])]});
            var Q15;
            Q15=makeQuery(id+"F1.opExtrude","SWEPT_BODY",BODY,{"disambiguationData":[OSD([sQuery(id+"F0.wireOp",EDGE,"E46"),sQuery(id+"F0.wireOp",EDGE,"E47"),sQuery(id+"F0.wireOp",EDGE,"E54.trimOffspring")])]});
            var Q16;
            Q16=makeQuery(id+"F1.opExtrude","SWEPT_BODY",BODY,{"disambiguationData":[OSD([sQuery(id+"F0.wireOp",EDGE,"E48"),sQuery(id+"F0.wireOp",EDGE,"E49"),sQuery(id+"F0.wireOp",EDGE,"E52.trimOffspring")])]});
            var Q17;
            Q17=makeQuery(id+"F4.opExtrude","SWEPT_BODY",BODY,{"disambiguationData":[OSD([sQuery(id+"F3.wireOp",EDGE,"E58.bottom"),sQuery(id+"F3.wireOp",EDGE,"E58.top"),sQuery(id+"F3.wireOp",EDGE,"E58.left"),sQuery(id+"F3.wireOp",EDGE,"E58.right")])]});
            booleanBodies(context, id + "F7", {"operationType" : BooleanOperationType.UNION, "tools" : qUnion([Q0, Q1, Q2, Q3, Q4, Q5, Q6, Q7, Q8, Q9, Q10, Q11, Q12, Q13, Q14, Q15, Q16, Q17])});
        }
        {
            var Q0;
            Q0=makeQuery(id+"F1.opExtrude","SWEPT_BODY",BODY,{"disambiguationData":[OSD([sQuery(id+"F0.wireOp",EDGE,"E1"),sQuery(id+"F0.wireOp",EDGE,"E2"),sQuery(id+"F0.wireOp",EDGE,"E3"),sQuery(id+"F0.wireOp",EDGE,"E4"),sQuery(id+"F0.wireOp",EDGE,"E5"),sQuery(id+"F0.wireOp",EDGE,"E6"),sQuery(id+"F0.wireOp",EDGE,"E7"),sQuery(id+"F0.wireOp",EDGE,"E8")])]});
            var Q1;
            Q1=makeQuery(id+"F4.opExtrude","CAP_EDGE",EDGE,{"disambiguationData":[OSD([sQuery(id+"F3.wireOp",EDGE,"E58.bottom")])],"isStart":true});
            transform(context, id + "F8", {"entities" : qUnion([Q0]), "transformType" : TransformType.ROTATION, "transformAxis" : qUnion([Q1]), "angle" : 180 * degree, "makeCopy" : false});
        }
        {
            var Q0;
            Q0=makeQuery(id+"F7.opBoolean","INTERSECT",EDGE,{"derivedFrom":[makeQuery(id+"F1.opExtrude","SWEPT_FACE",FACE,{"disambiguationData":[OSD([sQuery(id+"F0.wireOp",EDGE,"E5")])]}),makeQuery(id+"F4.opExtrude","CAP_FACE",FACE,{"disambiguationData":[OSD([sQuery(id+"F3.wireOp",EDGE,"E58.bottom"),sQuery(id+"F3.wireOp",EDGE,"E58.top"),sQuery(id+"F3.wireOp",EDGE,"E58.left"),sQuery(id+"F3.wireOp",EDGE,"E58.right")])],"isStart":false})]});
            var Q1;
            Q1=makeQuery(id+"F7.opBoolean","INTERSECT",EDGE,{"derivedFrom":[makeQuery(id+"F1.opExtrude","SWEPT_FACE",FACE,{"disambiguationData":[OSD([sQuery(id+"F0.wireOp",EDGE,"E6")])]}),makeQuery(id+"F4.opExtrude","CAP_FACE",FACE,{"disambiguationData":[OSD([sQuery(id+"F3.wireOp",EDGE,"E58.bottom"),sQuery(id+"F3.wireOp",EDGE,"E58.top"),sQuery(id+"F3.wireOp",EDGE,"E58.left"),sQuery(id+"F3.wireOp",EDGE,"E58.right")])],"isStart":false})]});
            var Q2;
            Q2=makeQuery(id+"F7.opBoolean","INTERSECT",EDGE,{"derivedFrom":[makeQuery(id+"F1.opExtrude","SWEPT_FACE",FACE,{"disambiguationData":[OSD([sQuery(id+"F0.wireOp",EDGE,"E7")])]}),makeQuery(id+"F4.opExtrude","CAP_FACE",FACE,{"disambiguationData":[OSD([sQuery(id+"F3.wireOp",EDGE,"E58.bottom"),sQuery(id+"F3.wireOp",EDGE,"E58.top"),sQuery(id+"F3.wireOp",EDGE,"E58.left"),sQuery(id+"F3.wireOp",EDGE,"E58.right")])],"isStart":false})]});
            var Q3;
            Q3=makeQuery(id+"F7.opBoolean","INTERSECT",EDGE,{"derivedFrom":[makeQuery(id+"F1.opExtrude","SWEPT_FACE",FACE,{"disambiguationData":[OSD([sQuery(id+"F0.wireOp",EDGE,"E4")])]}),makeQuery(id+"F4.opExtrude","CAP_FACE",FACE,{"disambiguationData":[OSD([sQuery(id+"F3.wireOp",EDGE,"E58.bottom"),sQuery(id+"F3.wireOp",EDGE,"E58.top"),sQuery(id+"F3.wireOp",EDGE,"E58.left"),sQuery(id+"F3.wireOp",EDGE,"E58.right")])],"isStart":false})]});
            var Q4;
            Q4=makeQuery(id+"F7.opBoolean","INTERSECT",EDGE,{"derivedFrom":[makeQuery(id+"F1.opExtrude","SWEPT_FACE",FACE,{"disambiguationData":[OSD([sQuery(id+"F0.wireOp",EDGE,"E3")])]}),makeQuery(id+"F4.opExtrude","CAP_FACE",FACE,{"disambiguationData":[OSD([sQuery(id+"F3.wireOp",EDGE,"E58.bottom"),sQuery(id+"F3.wireOp",EDGE,"E58.top"),sQuery(id+"F3.wireOp",EDGE,"E58.left"),sQuery(id+"F3.wireOp",EDGE,"E58.right")])],"isStart":false})]});
            var Q5;
            Q5=makeQuery(id+"F7.opBoolean","INTERSECT",EDGE,{"derivedFrom":[makeQuery(id+"F1.opExtrude","SWEPT_FACE",FACE,{"disambiguationData":[OSD([sQuery(id+"F0.wireOp",EDGE,"E2")])]}),makeQuery(id+"F4.opExtrude","CAP_FACE",FACE,{"disambiguationData":[OSD([sQuery(id+"F3.wireOp",EDGE,"E58.bottom"),sQuery(id+"F3.wireOp",EDGE,"E58.top"),sQuery(id+"F3.wireOp",EDGE,"E58.left"),sQuery(id+"F3.wireOp",EDGE,"E58.right")])],"isStart":false})]});
            var Q6;
            Q6=makeQuery(id+"F7.opBoolean","INTERSECT",EDGE,{"derivedFrom":[makeQuery(id+"F1.opExtrude","SWEPT_FACE",FACE,{"disambiguationData":[OSD([sQuery(id+"F0.wireOp",EDGE,"E8")])]}),makeQuery(id+"F4.opExtrude","CAP_FACE",FACE,{"disambiguationData":[OSD([sQuery(id+"F3.wireOp",EDGE,"E58.bottom"),sQuery(id+"F3.wireOp",EDGE,"E58.top"),sQuery(id+"F3.wireOp",EDGE,"E58.left"),sQuery(id+"F3.wireOp",EDGE,"E58.right")])],"isStart":false})]});
            var Q7;
            Q7=makeQuery(id+"F7.opBoolean","INTERSECT",EDGE,{"derivedFrom":[makeQuery(id+"F1.opExtrude","SWEPT_FACE",FACE,{"disambiguationData":[OSD([sQuery(id+"F0.wireOp",EDGE,"E1")])]}),makeQuery(id+"F4.opExtrude","CAP_FACE",FACE,{"disambiguationData":[OSD([sQuery(id+"F3.wireOp",EDGE,"E58.bottom"),sQuery(id+"F3.wireOp",EDGE,"E58.top"),sQuery(id+"F3.wireOp",EDGE,"E58.left"),sQuery(id+"F3.wireOp",EDGE,"E58.right")])],"isStart":false})]});
            var Q8;
            Q8=makeQuery(id+"F7.opBoolean","INTERSECT",EDGE,{"derivedFrom":[makeQuery(id+"F1.opExtrude","SWEPT_FACE",FACE,{"disambiguationData":[OSD([sQuery(id+"F0.wireOp",EDGE,"E10.filletArc")])]}),makeQuery(id+"F4.opExtrude","CAP_FACE",FACE,{"disambiguationData":[OSD([sQuery(id+"F3.wireOp",EDGE,"E58.bottom"),sQuery(id+"F3.wireOp",EDGE,"E58.top"),sQuery(id+"F3.wireOp",EDGE,"E58.left"),sQuery(id+"F3.wireOp",EDGE,"E58.right")])],"isStart":false})]});
            var Q9;
            Q9=makeQuery(id+"F7.opBoolean","INTERSECT",EDGE,{"derivedFrom":[makeQuery(id+"F1.opExtrude","SWEPT_FACE",FACE,{"disambiguationData":[OSD([sQuery(id+"F0.wireOp",EDGE,"E12.filletArc")])]}),makeQuery(id+"F4.opExtrude","CAP_FACE",FACE,{"disambiguationData":[OSD([sQuery(id+"F3.wireOp",EDGE,"E58.bottom"),sQuery(id+"F3.wireOp",EDGE,"E58.top"),sQuery(id+"F3.wireOp",EDGE,"E58.left"),sQuery(id+"F3.wireOp",EDGE,"E58.right")])],"isStart":false})]});
            var Q10;
            Q10=makeQuery(id+"F7.opBoolean","INTERSECT",EDGE,{"derivedFrom":[makeQuery(id+"F1.opExtrude","SWEPT_FACE",FACE,{"disambiguationData":[OSD([sQuery(id+"F0.wireOp",EDGE,"E11.top")])]}),makeQuery(id+"F4.opExtrude","CAP_FACE",FACE,{"disambiguationData":[OSD([sQuery(id+"F3.wireOp",EDGE,"E58.bottom"),sQuery(id+"F3.wireOp",EDGE,"E58.top"),sQuery(id+"F3.wireOp",EDGE,"E58.left"),sQuery(id+"F3.wireOp",EDGE,"E58.right")])],"isStart":false})]});
            var Q11;
            Q11=makeQuery(id+"F7.opBoolean","INTERSECT",EDGE,{"derivedFrom":[makeQuery(id+"F1.opExtrude","SWEPT_FACE",FACE,{"disambiguationData":[OSD([sQuery(id+"F0.wireOp",EDGE,"E9.top")])]}),makeQuery(id+"F4.opExtrude","CAP_FACE",FACE,{"disambiguationData":[OSD([sQuery(id+"F3.wireOp",EDGE,"E58.bottom"),sQuery(id+"F3.wireOp",EDGE,"E58.top"),sQuery(id+"F3.wireOp",EDGE,"E58.left"),sQuery(id+"F3.wireOp",EDGE,"E58.right")])],"isStart":false})]});
            var Q12;
            Q12=makeQuery(id+"F7.opBoolean","INTERSECT",EDGE,{"derivedFrom":[makeQuery(id+"F1.opExtrude","SWEPT_FACE",FACE,{"disambiguationData":[OSD([sQuery(id+"F0.wireOp",EDGE,"E11.right")])]}),makeQuery(id+"F4.opExtrude","CAP_FACE",FACE,{"disambiguationData":[OSD([sQuery(id+"F3.wireOp",EDGE,"E58.bottom"),sQuery(id+"F3.wireOp",EDGE,"E58.top"),sQuery(id+"F3.wireOp",EDGE,"E58.left"),sQuery(id+"F3.wireOp",EDGE,"E58.right")])],"isStart":false})]});
            var Q13;
            Q13=makeQuery(id+"F7.opBoolean","INTERSECT",EDGE,{"derivedFrom":[makeQuery(id+"F1.opExtrude","SWEPT_FACE",FACE,{"disambiguationData":[OSD([sQuery(id+"F0.wireOp",EDGE,"E11.bottom")])]}),makeQuery(id+"F4.opExtrude","CAP_FACE",FACE,{"disambiguationData":[OSD([sQuery(id+"F3.wireOp",EDGE,"E58.bottom"),sQuery(id+"F3.wireOp",EDGE,"E58.top"),sQuery(id+"F3.wireOp",EDGE,"E58.left"),sQuery(id+"F3.wireOp",EDGE,"E58.right")])],"isStart":false})]});
            var Q14;
            Q14=makeQuery(id+"F7.opBoolean","INTERSECT",EDGE,{"derivedFrom":[makeQuery(id+"F1.opExtrude","SWEPT_FACE",FACE,{"disambiguationData":[OSD([sQuery(id+"F0.wireOp",EDGE,"E9.bottom")])]}),makeQuery(id+"F4.opExtrude","CAP_FACE",FACE,{"disambiguationData":[OSD([sQuery(id+"F3.wireOp",EDGE,"E58.bottom"),sQuery(id+"F3.wireOp",EDGE,"E58.top"),sQuery(id+"F3.wireOp",EDGE,"E58.left"),sQuery(id+"F3.wireOp",EDGE,"E58.right")])],"isStart":false})]});
            var Q15;
            Q15=makeQuery(id+"F7.opBoolean","INTERSECT",EDGE,{"derivedFrom":[makeQuery(id+"F1.opExtrude","SWEPT_FACE",FACE,{"disambiguationData":[OSD([sQuery(id+"F0.wireOp",EDGE,"E9.right")])]}),makeQuery(id+"F4.opExtrude","CAP_FACE",FACE,{"disambiguationData":[OSD([sQuery(id+"F3.wireOp",EDGE,"E58.bottom"),sQuery(id+"F3.wireOp",EDGE,"E58.top"),sQuery(id+"F3.wireOp",EDGE,"E58.left"),sQuery(id+"F3.wireOp",EDGE,"E58.right")])],"isStart":false})]});
            var Q16;
            Q16=makeQuery(id+"F7.opBoolean","INTERSECT",EDGE,{"derivedFrom":[makeQuery(id+"F1.opExtrude","SWEPT_FACE",FACE,{"disambiguationData":[OSD([sQuery(id+"F0.wireOp",EDGE,"E11.left")])]}),makeQuery(id+"F4.opExtrude","CAP_FACE",FACE,{"disambiguationData":[OSD([sQuery(id+"F3.wireOp",EDGE,"E58.bottom"),sQuery(id+"F3.wireOp",EDGE,"E58.top"),sQuery(id+"F3.wireOp",EDGE,"E58.left"),sQuery(id+"F3.wireOp",EDGE,"E58.right")])],"isStart":false})]});
            var Q17;
            Q17=makeQuery(id+"F7.opBoolean","INTERSECT",EDGE,{"derivedFrom":[makeQuery(id+"F1.opExtrude","SWEPT_FACE",FACE,{"disambiguationData":[OSD([sQuery(id+"F0.wireOp",EDGE,"E13.left")])]}),makeQuery(id+"F4.opExtrude","CAP_FACE",FACE,{"disambiguationData":[OSD([sQuery(id+"F3.wireOp",EDGE,"E58.bottom"),sQuery(id+"F3.wireOp",EDGE,"E58.top"),sQuery(id+"F3.wireOp",EDGE,"E58.left"),sQuery(id+"F3.wireOp",EDGE,"E58.right")])],"isStart":false})]});
            var Q18;
            Q18=makeQuery(id+"F7.opBoolean","INTERSECT",EDGE,{"derivedFrom":[makeQuery(id+"F1.opExtrude","SWEPT_FACE",FACE,{"disambiguationData":[OSD([sQuery(id+"F0.wireOp",EDGE,"E14"),sQuery(id+"F0.wireOp",EDGE,"E17.left")])]}),makeQuery(id+"F4.opExtrude","CAP_FACE",FACE,{"disambiguationData":[OSD([sQuery(id+"F3.wireOp",EDGE,"E58.bottom"),sQuery(id+"F3.wireOp",EDGE,"E58.top"),sQuery(id+"F3.wireOp",EDGE,"E58.left"),sQuery(id+"F3.wireOp",EDGE,"E58.right")])],"isStart":false})]});
            var Q19;
            Q19=makeQuery(id+"F7.opBoolean","INTERSECT",EDGE,{"derivedFrom":[makeQuery(id+"F1.opExtrude","SWEPT_FACE",FACE,{"disambiguationData":[OSD([sQuery(id+"F0.wireOp",EDGE,"E13.bottom")])]}),makeQuery(id+"F4.opExtrude","CAP_FACE",FACE,{"disambiguationData":[OSD([sQuery(id+"F3.wireOp",EDGE,"E58.bottom"),sQuery(id+"F3.wireOp",EDGE,"E58.top"),sQuery(id+"F3.wireOp",EDGE,"E58.left"),sQuery(id+"F3.wireOp",EDGE,"E58.right")])],"isStart":false})]});
            var Q20;
            Q20=makeQuery(id+"F7.opBoolean","INTERSECT",EDGE,{"derivedFrom":[makeQuery(id+"F1.opExtrude","SWEPT_FACE",FACE,{"disambiguationData":[OSD([sQuery(id+"F0.wireOp",EDGE,"E13.top")])]}),makeQuery(id+"F4.opExtrude","CAP_FACE",FACE,{"disambiguationData":[OSD([sQuery(id+"F3.wireOp",EDGE,"E58.bottom"),sQuery(id+"F3.wireOp",EDGE,"E58.top"),sQuery(id+"F3.wireOp",EDGE,"E58.left"),sQuery(id+"F3.wireOp",EDGE,"E58.right")])],"isStart":false})]});
            var Q21;
            Q21=makeQuery(id+"F7.opBoolean","INTERSECT",EDGE,{"derivedFrom":[makeQuery(id+"F1.opExtrude","SWEPT_FACE",FACE,{"disambiguationData":[OSD([sQuery(id+"F0.wireOp",EDGE,"E15")])]}),makeQuery(id+"F4.opExtrude","CAP_FACE",FACE,{"disambiguationData":[OSD([sQuery(id+"F3.wireOp",EDGE,"E58.bottom"),sQuery(id+"F3.wireOp",EDGE,"E58.top"),sQuery(id+"F3.wireOp",EDGE,"E58.left"),sQuery(id+"F3.wireOp",EDGE,"E58.right")])],"isStart":false})]});
            var Q22;
            Q22=makeQuery(id+"F7.opBoolean","INTERSECT",EDGE,{"derivedFrom":[makeQuery(id+"F1.opExtrude","SWEPT_FACE",FACE,{"disambiguationData":[OSD([sQuery(id+"F0.wireOp",EDGE,"E17.bottom")])]}),makeQuery(id+"F4.opExtrude","CAP_FACE",FACE,{"disambiguationData":[OSD([sQuery(id+"F3.wireOp",EDGE,"E58.bottom"),sQuery(id+"F3.wireOp",EDGE,"E58.top"),sQuery(id+"F3.wireOp",EDGE,"E58.left"),sQuery(id+"F3.wireOp",EDGE,"E58.right")])],"isStart":false})]});
            var Q23;
            Q23=makeQuery(id+"F7.opBoolean","INTERSECT",EDGE,{"derivedFrom":[makeQuery(id+"F1.opExtrude","SWEPT_FACE",FACE,{"disambiguationData":[OSD([sQuery(id+"F0.wireOp",EDGE,"E18.filletArc"),sQuery(id+"F0.wireOp",EDGE,"E19.filletArc")])]}),makeQuery(id+"F4.opExtrude","CAP_FACE",FACE,{"disambiguationData":[OSD([sQuery(id+"F3.wireOp",EDGE,"E58.bottom"),sQuery(id+"F3.wireOp",EDGE,"E58.top"),sQuery(id+"F3.wireOp",EDGE,"E58.left"),sQuery(id+"F3.wireOp",EDGE,"E58.right")])],"isStart":false})]});
            var Q24;
            Q24=makeQuery(id+"F7.opBoolean","INTERSECT",EDGE,{"derivedFrom":[makeQuery(id+"F1.opExtrude","SWEPT_FACE",FACE,{"disambiguationData":[OSD([sQuery(id+"F0.wireOp",EDGE,"E16")])]}),makeQuery(id+"F4.opExtrude","CAP_FACE",FACE,{"disambiguationData":[OSD([sQuery(id+"F3.wireOp",EDGE,"E58.bottom"),sQuery(id+"F3.wireOp",EDGE,"E58.top"),sQuery(id+"F3.wireOp",EDGE,"E58.left"),sQuery(id+"F3.wireOp",EDGE,"E58.right")])],"isStart":false})]});
            fillet(context, id + "F9", {"entities" : qUnion([Q0, Q1, Q2, Q3, Q4, Q5, Q6, Q7, Q8, Q9, Q10, Q11, Q12, Q13, Q14, Q15, Q16, Q17, Q18, Q19, Q20, Q21, Q22, Q23, Q24]), "radius" : 0.1 * mm, "tangentPropagation" : true, "allowEdgeOverflow" : false});
        }
        {
            var Q0;
            Q0=makeQuery(id+"F1.opExtrude","SWEPT_BODY",BODY,{"disambiguationData":[OSD([sQuery(id+"F0.wireOp",EDGE,"E1"),sQuery(id+"F0.wireOp",EDGE,"E2"),sQuery(id+"F0.wireOp",EDGE,"E3"),sQuery(id+"F0.wireOp",EDGE,"E4"),sQuery(id+"F0.wireOp",EDGE,"E5"),sQuery(id+"F0.wireOp",EDGE,"E6"),sQuery(id+"F0.wireOp",EDGE,"E7"),sQuery(id+"F0.wireOp",EDGE,"E8")])]});
            transform(context, id + "F10", {"entities" : qUnion([Q0]), "transformType" : TransformType.TRANSLATION_3D, "dx" : 0 * mm, "dy" : 0 * mm, "dz" : -13.1 * mm, "makeCopy" : false});
        }
        {
            var Q0;
            Q0=makeQuery(id+"F1.opExtrude","SWEPT_BODY",BODY,{"disambiguationData":[OSD([sQuery(id+"F0.wireOp",EDGE,"E1"),sQuery(id+"F0.wireOp",EDGE,"E2"),sQuery(id+"F0.wireOp",EDGE,"E3"),sQuery(id+"F0.wireOp",EDGE,"E4"),sQuery(id+"F0.wireOp",EDGE,"E5"),sQuery(id+"F0.wireOp",EDGE,"E6"),sQuery(id+"F0.wireOp",EDGE,"E7"),sQuery(id+"F0.wireOp",EDGE,"E8")])]});
            transform(context, id + "F11", {"entities" : qUnion([Q0]), "transformType" : TransformType.TRANSLATION_3D, "dx" : 0 * mm, "dy" : -10 * mm, "dz" : 0 * mm, "makeCopy" : false});
        }
        {
            var Q0;
            Q0=makeQuery(id+"F7.opBoolean","INTERSECT",EDGE,{"derivedFrom":[makeQuery(id+"F1.opExtrude","SWEPT_FACE",FACE,{"disambiguationData":[OSD([sQuery(id+"F0.wireOp",EDGE,"E20.top")])]}),makeQuery(id+"F4.opExtrude","CAP_FACE",FACE,{"disambiguationData":[OSD([sQuery(id+"F3.wireOp",EDGE,"E58.bottom"),sQuery(id+"F3.wireOp",EDGE,"E58.top"),sQuery(id+"F3.wireOp",EDGE,"E58.left"),sQuery(id+"F3.wireOp",EDGE,"E58.right")])],"isStart":false})]});
            var Q1;
            Q1=makeQuery(id+"F7.opBoolean","INTERSECT",EDGE,{"derivedFrom":[makeQuery(id+"F1.opExtrude","SWEPT_FACE",FACE,{"disambiguationData":[OSD([sQuery(id+"F0.wireOp",EDGE,"E20.left")])]}),makeQuery(id+"F4.opExtrude","CAP_FACE",FACE,{"disambiguationData":[OSD([sQuery(id+"F3.wireOp",EDGE,"E58.bottom"),sQuery(id+"F3.wireOp",EDGE,"E58.top"),sQuery(id+"F3.wireOp",EDGE,"E58.left"),sQuery(id+"F3.wireOp",EDGE,"E58.right")])],"isStart":false})]});
            var Q2;
            Q2=makeQuery(id+"F7.opBoolean","INTERSECT",EDGE,{"derivedFrom":[makeQuery(id+"F1.opExtrude","SWEPT_FACE",FACE,{"disambiguationData":[OSD([sQuery(id+"F0.wireOp",EDGE,"E22.top")])]}),makeQuery(id+"F4.opExtrude","CAP_FACE",FACE,{"disambiguationData":[OSD([sQuery(id+"F3.wireOp",EDGE,"E58.bottom"),sQuery(id+"F3.wireOp",EDGE,"E58.top"),sQuery(id+"F3.wireOp",EDGE,"E58.left"),sQuery(id+"F3.wireOp",EDGE,"E58.right")])],"isStart":false})]});
            var Q3;
            Q3=makeQuery(id+"F7.opBoolean","INTERSECT",EDGE,{"derivedFrom":[makeQuery(id+"F1.opExtrude","SWEPT_FACE",FACE,{"disambiguationData":[OSD([sQuery(id+"F0.wireOp",EDGE,"E25.filletArc"),sQuery(id+"F0.wireOp",EDGE,"E26.filletArc")])]}),makeQuery(id+"F4.opExtrude","CAP_FACE",FACE,{"disambiguationData":[OSD([sQuery(id+"F3.wireOp",EDGE,"E58.bottom"),sQuery(id+"F3.wireOp",EDGE,"E58.top"),sQuery(id+"F3.wireOp",EDGE,"E58.left"),sQuery(id+"F3.wireOp",EDGE,"E58.right")])],"isStart":false})]});
            var Q4;
            Q4=makeQuery(id+"F7.opBoolean","INTERSECT",EDGE,{"derivedFrom":[makeQuery(id+"F1.opExtrude","SWEPT_FACE",FACE,{"disambiguationData":[OSD([sQuery(id+"F0.wireOp",EDGE,"E21.left"),sQuery(id+"F0.wireOp",EDGE,"E22.left")])]}),makeQuery(id+"F4.opExtrude","CAP_FACE",FACE,{"disambiguationData":[OSD([sQuery(id+"F3.wireOp",EDGE,"E58.bottom"),sQuery(id+"F3.wireOp",EDGE,"E58.top"),sQuery(id+"F3.wireOp",EDGE,"E58.left"),sQuery(id+"F3.wireOp",EDGE,"E58.right")])],"isStart":false})]});
            var Q5;
            Q5=makeQuery(id+"F7.opBoolean","INTERSECT",EDGE,{"derivedFrom":[makeQuery(id+"F1.opExtrude","SWEPT_FACE",FACE,{"disambiguationData":[OSD([sQuery(id+"F0.wireOp",EDGE,"E57.trimOffspring")])]}),makeQuery(id+"F4.opExtrude","CAP_FACE",FACE,{"disambiguationData":[OSD([sQuery(id+"F3.wireOp",EDGE,"E58.bottom"),sQuery(id+"F3.wireOp",EDGE,"E58.top"),sQuery(id+"F3.wireOp",EDGE,"E58.left"),sQuery(id+"F3.wireOp",EDGE,"E58.right")])],"isStart":false})]});
            var Q6;
            Q6=makeQuery(id+"F7.opBoolean","INTERSECT",EDGE,{"derivedFrom":[makeQuery(id+"F1.opExtrude","SWEPT_FACE",FACE,{"disambiguationData":[OSD([sQuery(id+"F0.wireOp",EDGE,"E52.trimOffspring")])]}),makeQuery(id+"F4.opExtrude","CAP_FACE",FACE,{"disambiguationData":[OSD([sQuery(id+"F3.wireOp",EDGE,"E58.bottom"),sQuery(id+"F3.wireOp",EDGE,"E58.top"),sQuery(id+"F3.wireOp",EDGE,"E58.left"),sQuery(id+"F3.wireOp",EDGE,"E58.right")])],"isStart":false})]});
            var Q7;
            Q7=makeQuery(id+"F7.opBoolean","INTERSECT",EDGE,{"derivedFrom":[makeQuery(id+"F1.opExtrude","SWEPT_FACE",FACE,{"disambiguationData":[OSD([sQuery(id+"F0.wireOp",EDGE,"E23.filletArc"),sQuery(id+"F0.wireOp",EDGE,"E24.filletArc")])]}),makeQuery(id+"F4.opExtrude","CAP_FACE",FACE,{"disambiguationData":[OSD([sQuery(id+"F3.wireOp",EDGE,"E58.bottom"),sQuery(id+"F3.wireOp",EDGE,"E58.top"),sQuery(id+"F3.wireOp",EDGE,"E58.left"),sQuery(id+"F3.wireOp",EDGE,"E58.right")])],"isStart":false})]});
            var Q8;
            Q8=makeQuery(id+"F7.opBoolean","INTERSECT",EDGE,{"derivedFrom":[makeQuery(id+"F1.opExtrude","SWEPT_FACE",FACE,{"disambiguationData":[OSD([sQuery(id+"F0.wireOp",EDGE,"E51.trimOffspring")])]}),makeQuery(id+"F4.opExtrude","CAP_FACE",FACE,{"disambiguationData":[OSD([sQuery(id+"F3.wireOp",EDGE,"E58.bottom"),sQuery(id+"F3.wireOp",EDGE,"E58.top"),sQuery(id+"F3.wireOp",EDGE,"E58.left"),sQuery(id+"F3.wireOp",EDGE,"E58.right")])],"isStart":false})]});
            var Q9;
            Q9=makeQuery(id+"F7.opBoolean","INTERSECT",EDGE,{"derivedFrom":[makeQuery(id+"F1.opExtrude","SWEPT_FACE",FACE,{"disambiguationData":[OSD([sQuery(id+"F0.wireOp",EDGE,"E33.trimOffspring")])]}),makeQuery(id+"F4.opExtrude","CAP_FACE",FACE,{"disambiguationData":[OSD([sQuery(id+"F3.wireOp",EDGE,"E58.bottom"),sQuery(id+"F3.wireOp",EDGE,"E58.top"),sQuery(id+"F3.wireOp",EDGE,"E58.left"),sQuery(id+"F3.wireOp",EDGE,"E58.right")])],"isStart":false})]});
            var Q10;
            Q10=makeQuery(id+"F7.opBoolean","INTERSECT",EDGE,{"derivedFrom":[makeQuery(id+"F1.opExtrude","SWEPT_FACE",FACE,{"disambiguationData":[OSD([sQuery(id+"F0.wireOp",EDGE,"E20.bottom")])]}),makeQuery(id+"F4.opExtrude","CAP_FACE",FACE,{"disambiguationData":[OSD([sQuery(id+"F3.wireOp",EDGE,"E58.bottom"),sQuery(id+"F3.wireOp",EDGE,"E58.top"),sQuery(id+"F3.wireOp",EDGE,"E58.left"),sQuery(id+"F3.wireOp",EDGE,"E58.right")])],"isStart":false})]});
            var Q11;
            Q11=makeQuery(id+"F7.opBoolean","INTERSECT",EDGE,{"derivedFrom":[makeQuery(id+"F1.opExtrude","SWEPT_FACE",FACE,{"disambiguationData":[OSD([sQuery(id+"F0.wireOp",EDGE,"E21.bottom")])]}),makeQuery(id+"F4.opExtrude","CAP_FACE",FACE,{"disambiguationData":[OSD([sQuery(id+"F3.wireOp",EDGE,"E58.bottom"),sQuery(id+"F3.wireOp",EDGE,"E58.top"),sQuery(id+"F3.wireOp",EDGE,"E58.left"),sQuery(id+"F3.wireOp",EDGE,"E58.right")])],"isStart":false})]});
            var Q12;
            Q12=makeQuery(id+"F7.opBoolean","INTERSECT",EDGE,{"derivedFrom":[makeQuery(id+"F1.opExtrude","SWEPT_FACE",FACE,{"disambiguationData":[OSD([sQuery(id+"F0.wireOp",EDGE,"E50.trimOffspring")])]}),makeQuery(id+"F4.opExtrude","CAP_FACE",FACE,{"disambiguationData":[OSD([sQuery(id+"F3.wireOp",EDGE,"E58.bottom"),sQuery(id+"F3.wireOp",EDGE,"E58.top"),sQuery(id+"F3.wireOp",EDGE,"E58.left"),sQuery(id+"F3.wireOp",EDGE,"E58.right")])],"isStart":false})]});
            var Q13;
            Q13=makeQuery(id+"F7.opBoolean","INTERSECT",EDGE,{"derivedFrom":[makeQuery(id+"F1.opExtrude","SWEPT_FACE",FACE,{"disambiguationData":[OSD([sQuery(id+"F0.wireOp",EDGE,"E27")])]}),makeQuery(id+"F4.opExtrude","CAP_FACE",FACE,{"disambiguationData":[OSD([sQuery(id+"F3.wireOp",EDGE,"E58.bottom"),sQuery(id+"F3.wireOp",EDGE,"E58.top"),sQuery(id+"F3.wireOp",EDGE,"E58.left"),sQuery(id+"F3.wireOp",EDGE,"E58.right")])],"isStart":false})]});
            var Q14;
            Q14=makeQuery(id+"F7.opBoolean","INTERSECT",EDGE,{"derivedFrom":[makeQuery(id+"F1.opExtrude","SWEPT_FACE",FACE,{"disambiguationData":[OSD([sQuery(id+"F0.wireOp",EDGE,"E56.trimOffspring")])]}),makeQuery(id+"F4.opExtrude","CAP_FACE",FACE,{"disambiguationData":[OSD([sQuery(id+"F3.wireOp",EDGE,"E58.bottom"),sQuery(id+"F3.wireOp",EDGE,"E58.top"),sQuery(id+"F3.wireOp",EDGE,"E58.left"),sQuery(id+"F3.wireOp",EDGE,"E58.right")])],"isStart":false})]});
            var Q15;
            Q15=makeQuery(id+"F7.opBoolean","INTERSECT",EDGE,{"derivedFrom":[makeQuery(id+"F1.opExtrude","SWEPT_FACE",FACE,{"disambiguationData":[OSD([sQuery(id+"F0.wireOp",EDGE,"E55.trimOffspring")])]}),makeQuery(id+"F4.opExtrude","CAP_FACE",FACE,{"disambiguationData":[OSD([sQuery(id+"F3.wireOp",EDGE,"E58.bottom"),sQuery(id+"F3.wireOp",EDGE,"E58.top"),sQuery(id+"F3.wireOp",EDGE,"E58.left"),sQuery(id+"F3.wireOp",EDGE,"E58.right")])],"isStart":false})]});
            var Q16;
            Q16=makeQuery(id+"F7.opBoolean","INTERSECT",EDGE,{"derivedFrom":[makeQuery(id+"F1.opExtrude","SWEPT_FACE",FACE,{"disambiguationData":[OSD([sQuery(id+"F0.wireOp",EDGE,"E54.trimOffspring")])]}),makeQuery(id+"F4.opExtrude","CAP_FACE",FACE,{"disambiguationData":[OSD([sQuery(id+"F3.wireOp",EDGE,"E58.bottom"),sQuery(id+"F3.wireOp",EDGE,"E58.top"),sQuery(id+"F3.wireOp",EDGE,"E58.left"),sQuery(id+"F3.wireOp",EDGE,"E58.right")])],"isStart":false})]});
            var Q17;
            Q17=makeQuery(id+"F7.opBoolean","INTERSECT",EDGE,{"derivedFrom":[makeQuery(id+"F1.opExtrude","SWEPT_FACE",FACE,{"disambiguationData":[OSD([sQuery(id+"F0.wireOp",EDGE,"E53.trimOffspring")])]}),makeQuery(id+"F4.opExtrude","CAP_FACE",FACE,{"disambiguationData":[OSD([sQuery(id+"F3.wireOp",EDGE,"E58.bottom"),sQuery(id+"F3.wireOp",EDGE,"E58.top"),sQuery(id+"F3.wireOp",EDGE,"E58.left"),sQuery(id+"F3.wireOp",EDGE,"E58.right")])],"isStart":false})]});
            var Q18;
            Q18=makeQuery(id+"F7.opBoolean","INTERSECT",EDGE,{"derivedFrom":[makeQuery(id+"F1.opExtrude","SWEPT_FACE",FACE,{"disambiguationData":[OSD([sQuery(id+"F0.wireOp",EDGE,"E20.right")])]}),makeQuery(id+"F4.opExtrude","CAP_FACE",FACE,{"disambiguationData":[OSD([sQuery(id+"F3.wireOp",EDGE,"E58.bottom"),sQuery(id+"F3.wireOp",EDGE,"E58.top"),sQuery(id+"F3.wireOp",EDGE,"E58.left"),sQuery(id+"F3.wireOp",EDGE,"E58.right")])],"isStart":false})]});
            fillet(context, id + "F12", {"entities" : qUnion([Q0, Q1, Q2, Q3, Q4, Q5, Q6, Q7, Q8, Q9, Q10, Q11, Q12, Q13, Q14, Q15, Q16, Q17, Q18]), "radius" : 0.1 * mm, "tangentPropagation" : true, "allowEdgeOverflow" : false});
        }
    });
